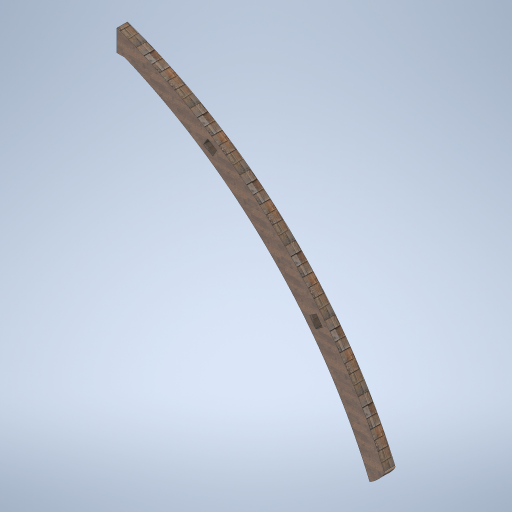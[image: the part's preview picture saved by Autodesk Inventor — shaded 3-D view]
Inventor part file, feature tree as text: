
AUTODESK INVENTOR PART (.ipt)
format: ipt  version: 2024.2 (Build 282272000, 272)  size: 336,896 bytes
history: native  units: mm
features: extrude x2, sketch x2, fillet x1
ambient origin geometry x8: Origin, YZ Plane, XZ Plane, XY Plane, X Axis, Y Axis, Z Axis, Center Point
bodies: Solid1 (feature_tree)
feature tree (5):
  extrude  "Extrusion1"  Depth=8500.0mm
  fillet  "Fillet2"  Radius=800.0mm
  extrude  "Extrusion3"  Depth=50.0mm
  sketch  "Sketch2"  dims[d5=8500.0mm d7=8500.0mm d8=800.0mm]
  sketch  "Sketch4"  dims[d9=100.0mm d10=100.0mm d11=0.0mm d12=0.0mm d15=50.0mm d16=200.0mm d17=30.0deg d18=150.0mm d19=200.0mm d20=9.599311mm d21=150.0mm d24=0.0mm d25=0.0mm]
